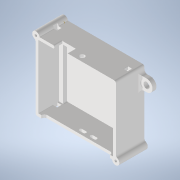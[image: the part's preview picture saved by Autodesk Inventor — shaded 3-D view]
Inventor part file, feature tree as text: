
AUTODESK INVENTOR PART (.ipt)
format: ipt  version: 2021.3 (Build 253353010, 353A)  size: 394,752 bytes
history: native  units: mm
features: extrude x9, sketch x7, projected_geometry x7, fillet x4, plane x1, other x1
ambient origin geometry x8: Origin, YZ Plane, XZ Plane, XY Plane, X Axis, Y Axis, Z Axis, Center Point
bodies: Volumenkörper1 (feature_tree)
feature tree (29):
  extrude  "boden"  Depth=64.8mm
  extrude  "waende"  Depth=4.0mm
  extrude  "led_u_usb"  Depth=3.0mm
  extrude  "kabellock"  TaperAngle=0.0deg  [1 undecoded]
  extrude  "boecke_platine"  Depth=16.7mm
  extrude  "platinenriegel"  Depth=25.0mm
  plane  "Arbeitsebene1"
  extrude  "befest"  Depth=4.0mm
  fillet  "Rundung1"  Radius=3.0mm
  extrude  "aussparung_schraubkopf_befest"  Depth=25.0mm
  fillet  "Rundung2"  [1 undecoded]
  fillet  "Rundung3"  Radius=2.5mm
  fillet  "Rundung4"  Radius=2.5mm
  extrude  "kabelbinderoesen"  Depth=2.5mm
  sketch  "Skizze1"  dims[d0=76.0mm d1=64.8mm]
  sketch  "Skizze2"  dims[d2=3.0mm d3=4.0mm]
  projected_geometry  "Projizierte Kontur1"
  projected_geometry  "Projizierte Kontur2"
  sketch  "Skizze4"  dims[d4=0.0mm d5=3.0mm]
  projected_geometry  "Projizierte Kontur3"
  sketch  "Skizze5"  dims[d6=25.0mm d7=0.0mm]
  projected_geometry  "Projizierte Kontur4"
  other  "platinenriegel_s"
  projected_geometry  "Projizierte Kontur5"
  sketch  "Skizze7"  dims[d9=13.0mm d10=16.7mm]
  sketch  "Skizze8"  dims[d11=25.0mm d12=0.0mm d13=39.5mm]
  sketch  "Skizze9"  dims[d14=5.0mm d15=5.0mm d16=3.0mm d17=25.0mm d18=0.0mm d19=2.5mm d20=2.5mm d21=2.5mm d22=2.5mm d23=3.0mm d24=3.0mm d25=3.0mm d26=3.0mm d27=4.0mm d28=4.0mm d29=4.0mm d30=0.0mm d31=1.7mm d32=4.5mm d33=0.0mm d34=0.0mm d35=0.0mm d36=13.0mm d37=3.0mm d38=6.2mm d39=3.0mm d40=4.0mm d41=0.0mm d42=3.0mm d43=11.0mm d45=11.0mm d46=4.0mm d47=0.0mm d48=2.0mm d49=1.0mm d50=0.3mm d51=0.5mm d52=7.0mm d53=3.0mm d54=50.0mm d55=7.0mm d56=3.0mm d57=4.0mm d58=4.0mm d59=4.0mm d60=0.0mm d81=22.5mm]
  projected_geometry  "Projizierte Kontur6"
  projected_geometry  "Projizierte Kontur7"
note: 2 required parameter values undecoded (feature->parameter linkage not recoverable at this tier; creation-order binding heuristic only, values carry confidence <= 0.55)
